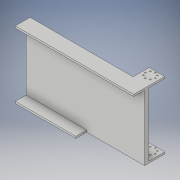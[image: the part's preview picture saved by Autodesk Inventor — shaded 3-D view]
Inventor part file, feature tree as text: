
AUTODESK INVENTOR PART (.ipt)
format: ipt  version: 2019 (Build 230136000, 136)  size: 181,760 bytes
history: native  units: in
note: dims shown in document units (in); Inventor stores cm internally (conversion verified against a paired STEP export)
features: extrude x6, sketch x6, plane x1, mirror x1
ambient origin geometry x8: Origin, YZ Plane, XZ Plane, XY Plane, X Axis, Y Axis, Z Axis, Center Point
bodies: Solid1 (feature_tree)
feature tree (14):
  extrude  "Extrusion1"  Depth=9.2in
  extrude  "Extrusion2"  Depth=0.151in
  extrude  "Extrusion3"  Depth=0.846in TaperAngle=0.0deg
  extrude  "Extrusion4"  Depth=0.151in
  extrude  "Extrusion7"  Depth=0.151in
  plane  "Work Plane1"
  mirror  "Mirror2"
  extrude  "Extrusion9"  Depth=0.151in
  sketch  "Sketch1"  dims[d0=5.223in d1=9.2in]
  sketch  "Sketch2"  dims[d2=1.15in d3=0.0in d4=0.151in]
  sketch  "Sketch3"  dims[d5=0.151in d6=0.846in d7=0.0in]
  sketch  "Sketch4"  dims[d8=4.5in d9=0.151in]
  sketch  "Sketch7"  dims[d10=0.846in d11=0.0in d12=0.151in]
  sketch  "Sketch9"  dims[d13=1.2in d14=0.151in d15=1.2in d16=1.25in d17=0.0in d39=0.2in d40=0.107in d41=0.385in d42=3.1496in d44=360.0deg d46=0.5in d47=0.0in d57=0.107in d58=0.766in d59=0.107in d60=1.5in d61=0.5in d62=0.0in]
